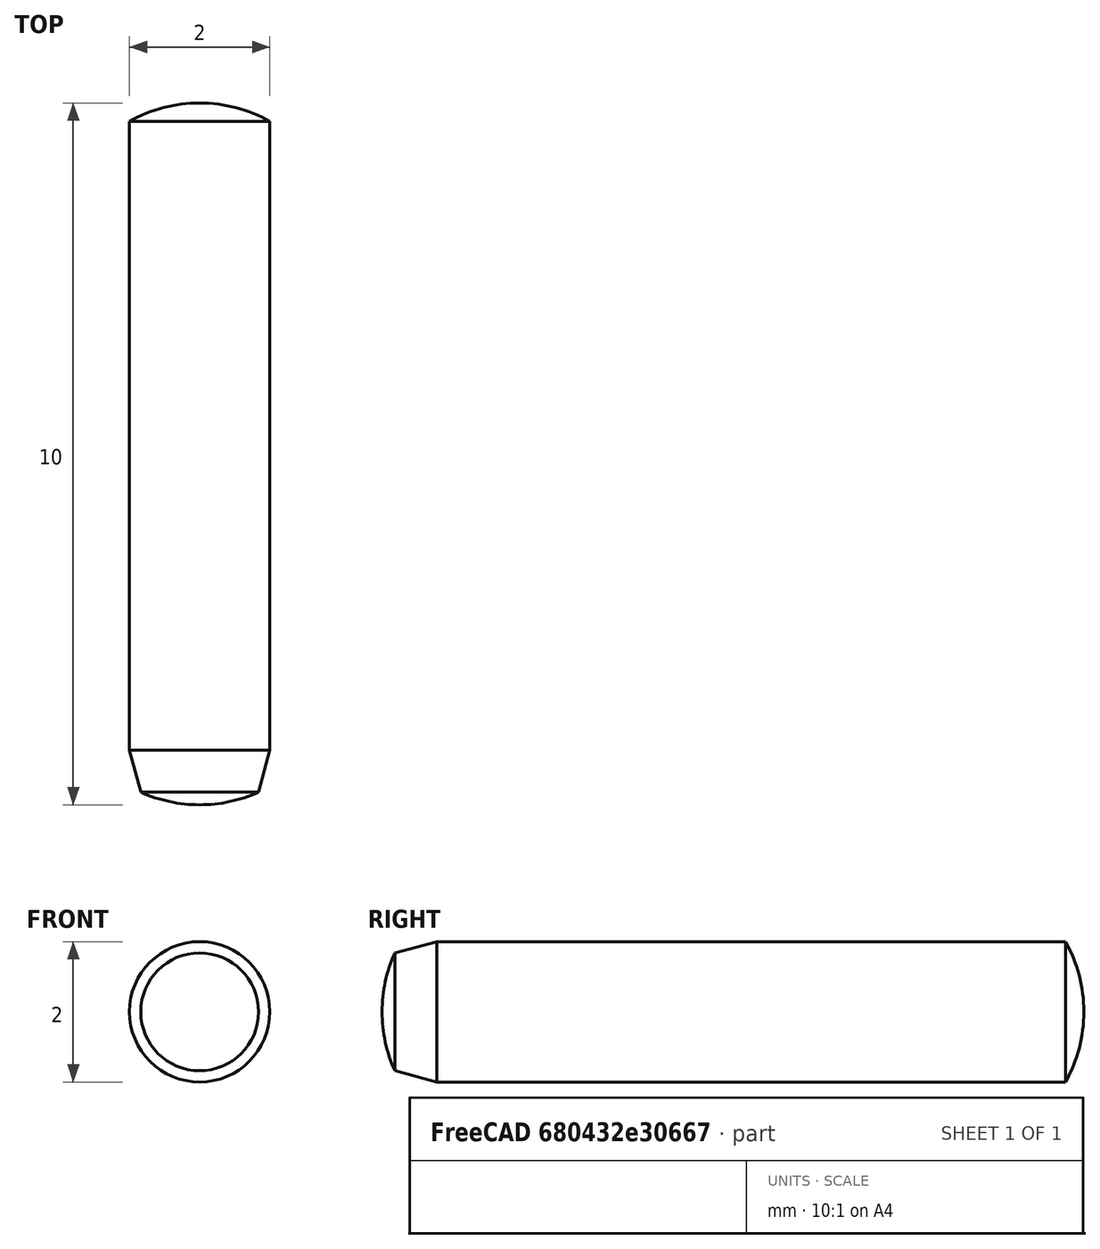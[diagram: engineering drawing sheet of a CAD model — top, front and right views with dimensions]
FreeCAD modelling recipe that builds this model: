
FCSTD DOCUMENT  (FreeCAD 0.15R4470 (Git))
Label: Zyl-Stift_DIN_6325-2x10
License: CC-BY 3.0
LicenseURL: http://creativecommons.org/licenses/by/3.0/
objects: Sketcher::SketchObject×1, PartDesign::Revolution×1
note: 3 computed .brp shape members not serialized (recipe doc carries the construction recipe); baked Part::Feature solids carry a one-line shape summary decoded from their .brp

FEATURE [Sketcher::SketchObject] Sketch
  Placement = pos=(0,0,0) rot=(0.57735,0.57735,0.57735;2.0944rad)
  sketch-geometry (5):
    g0: ArcOfCircle CenterX=1.86641 CenterY=0 CenterZ=0 NormalX=0 NormalY=0 NormalZ=1 Radius=2.04641 StartAngle=2.71903 EndAngle=3.14159
    g1: LineSegment StartX=0 StartY=0.83923 StartZ=0 EndX=0.6 EndY=1 EndZ=0
    g2: LineSegment StartX=0.6 StartY=1 StartZ=0 EndX=9.55903 EndY=1 EndZ=0
    g3: ArcOfCircle CenterX=7.77359 CenterY=0 CenterZ=0 NormalX=0 NormalY=0 NormalZ=1 Radius=2.04641 StartAngle=0 EndAngle=0.510554
    g4: LineSegment StartX=-0.18 StartY=0 StartZ=0 EndX=9.82 EndY=0 EndZ=0
  constraints (17):
    c: PointOnObject(g0,g-1)
    c: PointOnObject(g0,g-1)
    c: PointOnObject(g0,g-2)
    c: Coincident(g0,g1)
    c: Coincident(g1,g2)
    c: Horizontal(g2)
    c: PointOnObject(g3,g-1)
    c: Coincident(g3,g2)
    c: PointOnObject(g3,g-1)
    c: Coincident(g4,g0)
    c: Coincident(g4,g3)
    c: Equal(g0,g3)
    c: Angle(g4,g1) = 0.261799
    c: DistanceX(g4) = 10
    c: DistanceY(g-1,g1) = 1
    c: DistanceX(g1) = 0.6
    c: DistanceX(g0,g0) = 0.18
FEATURE [PartDesign::Revolution] Revolution  label="Zyl-Stift DIN 6325-2x10 #"
  Angle = 360
  Axis = (0,1,0)
  Base = (0,0,0)
  Placement = pos=(0,0,0) rot=(0.57735,0.57735,0.57735;2.0944rad)
  ReferenceAxis = -> Sketch [H_Axis]
  Sketch = -> Sketch
